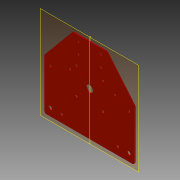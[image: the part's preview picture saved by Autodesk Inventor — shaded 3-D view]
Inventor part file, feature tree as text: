
AUTODESK INVENTOR PART (.ipt)
format: ipt  version: 2013 (Build 170138000, 138)  size: 196,608 bytes
history: native  units: in
note: dims shown in document units (in); Inventor stores cm internally (conversion verified against a paired STEP export)
features: extrude x7, sketch x7, pattern_linear x2, plane x2, fillet x1, mirror x1
ambient origin geometry x8: Origin, YZ Plane, XZ Plane, XY Plane, X Axis, Y Axis, Z Axis, Center Point
bodies: Solid1 (feature_tree)
feature tree (20):
  extrude  "Extrusion1"  Depth=2.3622in
  extrude  "Extrusion2"  Depth=3.5433in
  pattern_linear  "Rectangular Pattern1"  Count1=9  [1 undecoded]
  extrude  "Extrusion3"  Depth=0.0747in TaperAngle=0.0deg
  extrude  "Extrusion4"  Depth=0.5in
  extrude  "Extrusion5"  Depth=0.3937in
  extrude  "Extrusion6"  Depth=0.1969in
  pattern_linear  "Rectangular Pattern2"  Count1=2  [1 undecoded]
  fillet  "Fillet2"  Radius=0.5118in
  extrude  "Extrusion7"  Depth=3.1496in
  plane  "Work Plane1"
  plane  "Work Plane2"
  mirror  "Mirror1"
  sketch  "Sketch1"  dims[d0=6.2992in d4=2.3622in]
  sketch  "Sketch2"  dims[d5=1.9685in d6=3.5433in d7=3.5433in]
  sketch  "Sketch3"  dims[d8=5.9055in d9=0.0747in d10=0.0in]
  sketch  "Sketch4"  dims[d11=0.281in d12=0.5in]
  sketch  "Sketch5"  dims[d13=0.3937in d14=0.3937in]
  sketch  "Sketch6"  dims[d15=2.5433in d16=0.1969in]
  sketch  "Sketch7"  dims[d17=0.1345in d18=0.0in d19=0.7874in d21=5.5118in d22=0.5118in d23=3.1496in d24=3.0433in d25=0.1345in d26=0.0in d27=0.1181in d28=2.4333in d29=2.5396in d30=0.1181in d31=2.4333in d32=3.7596in d33=0.1181in d34=0.1181in d35=2.5396in d36=3.6533in d37=3.6533in d38=3.7596in d39=1.7717in d40=0.5in d41=0.1969in d42=1.378in d43=0.5in d44=0.1969in d45=0.1345in d46=0.0in d47=0.3937in d48=0.3937in d49=0.7874in d50=0.3937in d51=0.1969in d52=0.1969in d53=0.1345in d54=0.0in d55=2.22in d56=2.113in d57=0.2in d58=0.1345in d59=0.0in d60=0.7874in d62=1.86in d63=0.7874in d65=1.86in d67=0.125in d68=0.1969in d69=0.5in d70=1.1811in d71=0.1969in d72=1.1811in d73=0.5in d74=1.0in d75=0.0in]
note: 2 required parameter values undecoded (feature->parameter linkage not recoverable at this tier; creation-order binding heuristic only, values carry confidence <= 0.55)
